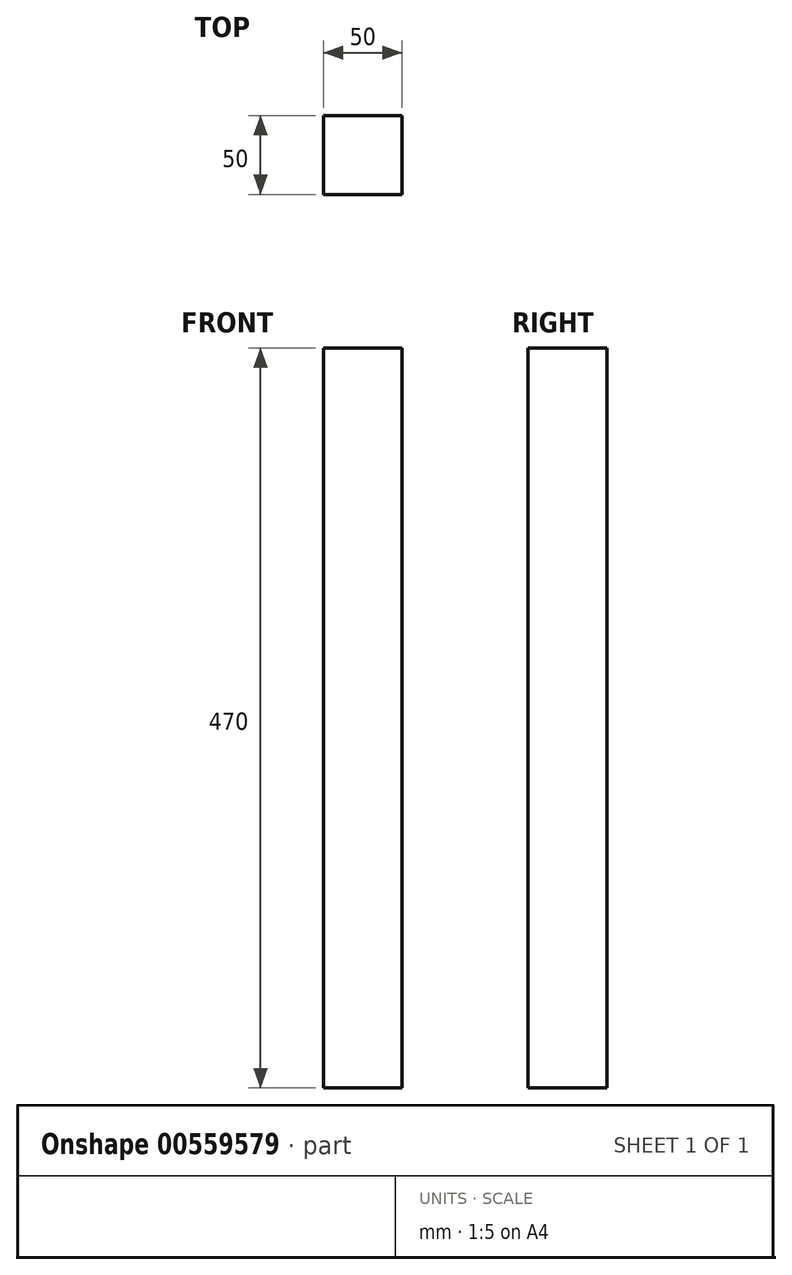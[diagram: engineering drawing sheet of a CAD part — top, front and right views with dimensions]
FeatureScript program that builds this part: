
annotation { "Feature Type Name" : "Feature", "Feature Type Description" : "" }
export const myFeature = defineFeature(function(context is Context, id is Id, definition is map)
    precondition{}
    {
        {
            var Q0;
            Q0=qCreatedBy(makeId("Front.planeOp"),FACE);
            var sketch = newSketch(context, id + "F0", { "sketchPlane" : qUnion([Q0])});
            skLineSegment(sketch, "E0.bottom", {"start": v(-60.02, 360.12) * mm, "end": v(-10.02, 360.12) * mm});
            skLineSegment(sketch, "E0.top", {"start": v(-60.02, -109.88) * mm, "end": v(-10.02, -109.88) * mm});
            skLineSegment(sketch, "E0.left", {"start": v(-60.02, 360.12) * mm, "end": v(-60.02, -109.88) * mm});
            skLineSegment(sketch, "E0.right", {"start": v(-10.02, 360.12) * mm, "end": v(-10.02, -109.88) * mm});
            skSolve(sketch);
        }
        {
            var Q0;
            Q0 = qSketchRegion(id + "F0", true);
            extrude(context, id + "F1", {"entities" : qUnion([Q0]), "depth" : 50 * mm, "offsetDistance" : 25 * mm});
        }
    });
